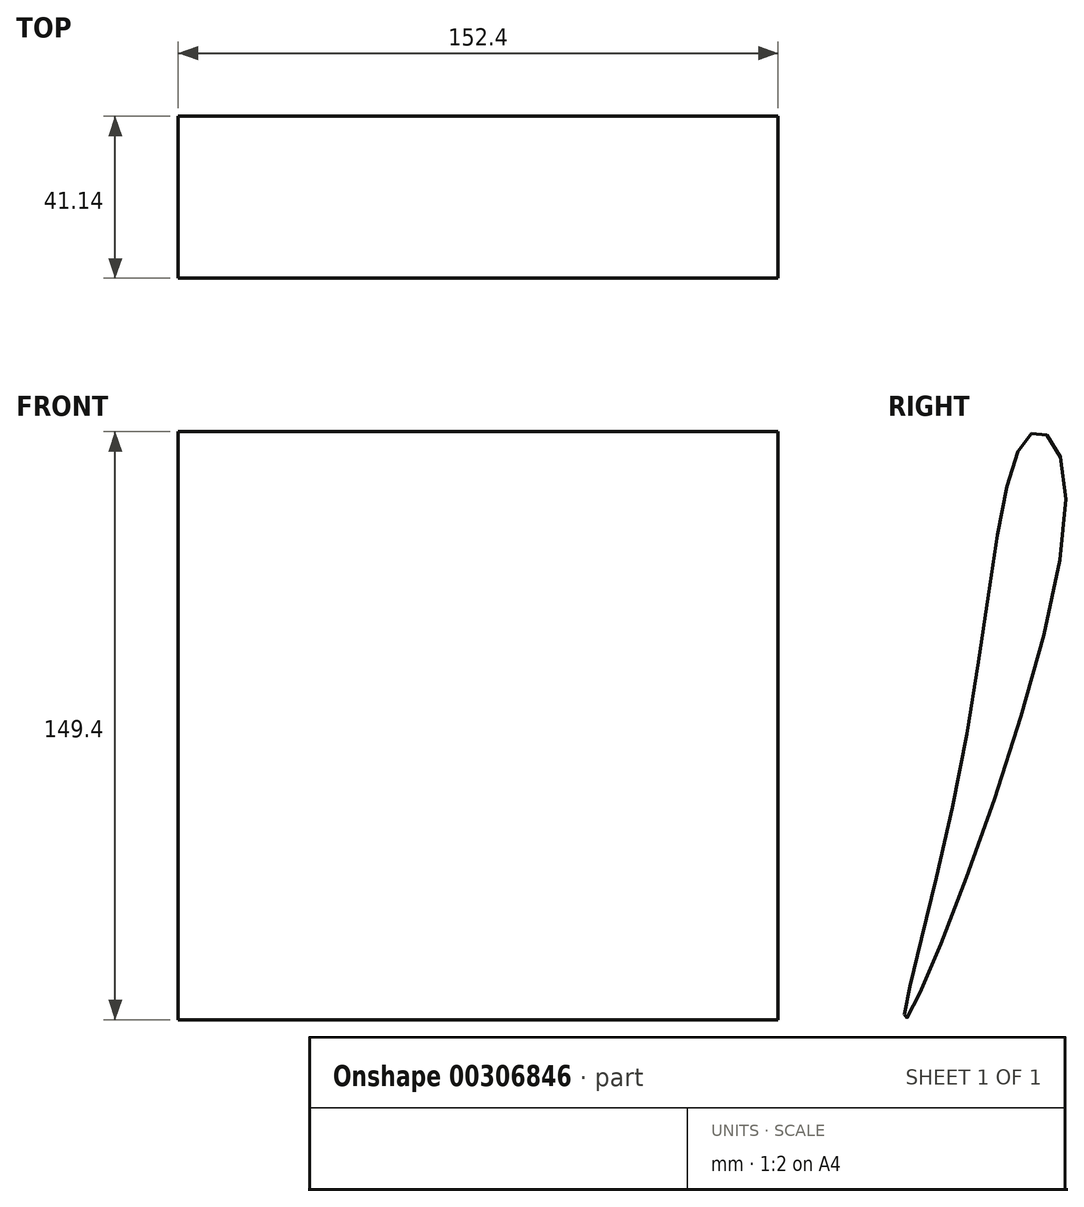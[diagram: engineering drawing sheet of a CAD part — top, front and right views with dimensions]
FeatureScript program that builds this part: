
annotation { "Feature Type Name" : "Feature", "Feature Type Description" : "" }
export const myFeature = defineFeature(function(context is Context, id is Id, definition is map)
    precondition{}
    {
        {
            var Q0;
            Q0=qCreatedBy(makeId("Right.planeOp"),FACE);
            var sketch = newSketch(context, id + "F0", { "sketchPlane" : qUnion([Q0])});
            skFitSpline(sketch, "E0", {"points": [v(29.53, 72.02) * mm, v(38.35, 56.81) * mm, v(-2.03, -76.46) * mm, v(12.04, -10.24) * mm, v(29.53, 72.02) * mm]});
            skSolve(sketch);
        }
        {
            var Q0;
            Q0=makeQuery(id+"F0.imprint","IMPRINT",FACE,{"disambiguationData":[TD([[makeQuery(id+"F0.imprint","IMPRINT",EDGE,{"derivedFrom":sQuery(id+"F0.wireOp",EDGE,"E0")}),-1.0]])]});
            extrude(context, id + "F1", {"entities" : qUnion([Q0]), "depth" : 76.2 * mm, "hasSecondDirection" : true, "secondDirectionOppositeDirection" : true, "secondDirectionDepth" : 76.2 * mm});
        }
    });
